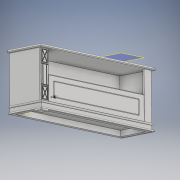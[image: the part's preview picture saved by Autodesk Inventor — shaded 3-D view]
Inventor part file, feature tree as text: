
AUTODESK INVENTOR PART (.ipt)
format: ipt  version: 2019 (Build 230136000, 136)  size: 589,824 bytes
history: native  units: mm
features: other x43, projected_geometry x15, sketch x10, extrude x8, fillet x6, shell x2, sweep x1
ambient origin geometry x8: Origin, YZ Plane, XZ Plane, XY Plane, X Axis, Y Axis, Z Axis, Center Point
bodies: Body1 (feature_tree), Body2 (feature_tree), Body3 (feature_tree), Body4 (feature_tree), Body5 (feature_tree), Body6 (feature_tree), Body7 (feature_tree), Body8 (feature_tree), Body9 (feature_tree), Body10 (feature_tree), Body11 (feature_tree), Body12 (feature_tree), Body13 (feature_tree)
feature tree (85):
  other  "Твердое тело1"
  other  "РабПлоскость3"
  other  "РабПлоскость1"
  other  "РабПлоскость4"
  extrude  "Выдавливание2"  Depth=630.0mm
  other  "РабПлоскость5"
  other  "Разделение3"
  other  "РабПлоскость6"
  other  "Разделение4"
  other  "РабПлоскость7"
  other  "Разделение5"
  other  "РабПлоскость8"
  other  "Разделение6"
  other  "РабПлоскость9"
  other  "РабПлоскость10"
  other  "Разделение7"
  other  "Разделение8"
  other  "Толщина1"
  other  "РабПлоскость11"
  other  "Разделение9"
  other  "Толщина2"
  shell  "Оболочка1"  Thickness=1996.0mm
  extrude  "Выдавливание4"  TaperAngle=0.0deg  [1 undecoded]
  fillet  "Сопряжение1"  [1 undecoded]
  extrude  "Выдавливание5"  [1 undecoded]
  other  "Толщина3"
  shell  "Оболочка3"  Thickness=-17.4mm
  extrude  "Выдавливание6"  [1 undecoded]
  fillet  "Сопряжение2"  [1 undecoded]
  extrude  "Выдавливание7"  [1 undecoded]
  fillet  "Сопряжение3"  Radius=2.0mm
  sketch  "Эскиз8"
  extrude  "Выдавливание11"  Depth=2.0mm
  extrude  "Выдавливание12"  [1 undecoded]
  other  "РабПлоскость12"
  fillet  "Сопряжение5"  Radius=2.0mm
  sketch  "Эскиз20"
  other  "РабПлоскость13"
  sketch  "Эскиз21"
  sweep  "Сдвиг2"
  other  "РабПлоскость14"
  extrude  "Выдавливание17"  Depth=70.0mm
  fillet  "Сопряжение6"  Radius=20.0mm
  other  "Толщина4"
  fillet  "Сопряжение7"  [1 undecoded]
  sketch  "Эскиз2"
  sketch  "Эскиз4"
  projected_geometry  "Спроецированная петля2"
  projected_geometry  "Спроецированная петля3"
  other  "ТВ Дно"
  sketch  "Эскиз5"
  projected_geometry  "Спроецированная петля4"
  projected_geometry  "Спроецированная петля5"
  other  "ТВ Цоколь"
  sketch  "Эскиз6"
  projected_geometry  "Спроецированная петля6"
  other  "ТВ Ножка"
  sketch  "Эскиз7"
  projected_geometry  "Спроецированная петля7"
  other  "ТВ Планка цоколя"
  projected_geometry  "Спроецированная петля8"
  sketch  "Эскиз10"
  projected_geometry  "Спроецированная петля10"
  projected_geometry  "Спроецированная петля11"
  projected_geometry  "Спроецированная петля12"
  projected_geometry  "Спроецированная петля13"
  other  "ТВ Полка"
  sketch  "Эскиз11"
  projected_geometry  "Спроецированная петля14"
  projected_geometry  "Спроецированная петля15"
  other  "ТВ Столешница"
  projected_geometry  "Спроецированная петля21"
  projected_geometry  "Спроецированная петля22"
  other  "Твердое тело6"
  other  "Твердое тело7"
  other  "ТВ Стенка боковая"
  other  "Твердое тело9"
  other  "Твердое тело10"
  other  "ТВ Стенка задняя"
  other  "ТВ Пилястра"
  other  "Твердое тело13"
  other  "Твердое тело14"
  other  "Твердое тело15"
  other  "ТВ Фасад ящика"
  other  "ТВ Дверца"
note: 8 required parameter values undecoded (feature->parameter linkage not recoverable at this tier; creation-order binding heuristic only, values carry confidence <= 0.55)
